# Revit family: НЕВАТОМ_Щит приточный, электрический калорифер, E, Версия 1
name_source: partatom
category: Электрооборудование
revit_build: Autodesk Revit 2017 (Build: 20170118_1100(x64)
units: mm (PartAtom-declared; Revit-internal decimal feet)

## family parameters
Всегда вертикально = Да
Заголовок OmniClass = Distribution Boards and Control Panels
Конфигурация панели = Два столбца, слева направо
На основе рабочей плоскости = Да
Номер OmniClass = 23.80.30.11.17
Общий = Нет
При загрузке вырезать с полостями = Нет
Размер круглого соединителя = Использовать диаметр
Тип детали = Щит
Точка расчета площади = Нет

## types (81) — shared parameters
ADSK_Единица измерения = шт.
ADSK_Завод-изготовитель = НЕВАТОМ
ADSK_Количество = 1
ADSK_Количество фаз = 3
ADSK_Материал = <По категории>
ф1 = 65 мм
ф2 = 144 мм
ф3 = 220 мм

## per-type parameters (varying)
| type | ADSK_Марка | ADSK_Наименование | ADSK_Напряжение | ADSK_Размер_Высота | ADSK_Размер_Длина | ADSK_Размер_Ширина | Количество ступеней нагревателя | Макс. допустимая мощность нагревателя, кВт | НЕВАТОМ_Номинальный ток двигателя | НЕВАТОМ_Ориентировочная мощность двигателя | НЕВАТОМ_Преобразователь частоты Danfoss, кВт | Отметка по умолчанию | видимость 1 | видимость 2 калорифер | видимость 3 ( 6 лампочек) | видимость 4 (4  лампочки) | видимость 5 ( 3 лампочки) | видимость 6 (5 лампочек) | кнопка |
| ABUm–Е–1–ZM-0,35-4,5/1 | ABUm–Е–1–ZM-0,35-4,5/1 | ABUm–Е–1–ZM-0,35-4,5/1 | 0 В | 650 мм | 400 мм | 200 мм | 1 мм | 4.5 | 0 А | 0 кВт |  | 1219 мм | Нет | Да | Нет | Нет | Нет | Нет | 10 мм |
| ABUm–Е–1–ZM-0,75-4,5/1 | ABUm–Е–1–ZM-0,75-4,5/1 | ABUm–Е–1–ZM-0,75-4,5/1 | 380 В | 650 мм | 400 мм | 200 мм | 1 мм | 4.5 | 0 А | 0 кВт |  | 1219 мм | Нет | Да | Нет | Нет | Нет | Нет | 10 мм |
| ABUm–E–1–ZM–0,35–6/1 | ABUm–E–1–ZM–0,35–6/1 | ABUm–E–1–ZM–0,35–6/1 | 380 В | 650 мм | 400 мм | 200 мм | 1 мм | 6 | 2 А | 0 кВт | ND–051 0,37 кВт для 3 фазы | 1219 мм | Нет | Да | Нет | Нет | Да | Нет | 10 мм |
| ABUm–E–1–ZM–0,75–6/1 | ABUm–E–1–ZM–0,75–6/1 | ABUm–E–1–ZM–0,75–6/1 | 380 В | 650 мм | 400 мм | 200 мм | 1 мм | 6 | 3 А | 0 кВт | ND–051 0,75 кВт для 3 фазы | 0 мм | Нет | Да | Нет | Нет | Да | Нет | 10 мм |
| ABUm–E–1–ZM–0,35–7,5/1 | ABUm–E–1–ZM–0,35–7,5/1 | ABUm–E–1–ZM–0,35–7,5/1 | 380 В | 650 мм | 400 мм | 300 мм | 1 мм | 7.5 | 2 А | 0 кВт | ND–051 0,37 кВт для 3 фазы | 1219 мм | Нет | Да | Нет | Нет | Да | Нет | 10 мм |
| ABUm–E–1–ZM–0,75–7,5/1 | ABUm–E–1–ZM–0,75–7,5/1 | ABUm–E–1–ZM–0,75–7,5/1 | 380 В | 650 мм | 400 мм | 200 мм | 1 мм | 7.5 | 0 А | 0 кВт |  | 1219 мм | Нет | Да | Нет | Нет | Да | Нет | 10 мм |
| ABUm–E–1–ZM–0,35–12/2 | ABUm–E–1–ZM–0,35–12/2 | ABUm–E–1–ZM–0,35–12/2 | 380 В | 650 мм | 400 мм | 200 мм | 2 мм | 12 | 2 А | 0 кВт | ND–051 0,37 кВт для 3 фазы | 1219 мм | Нет | Да | Нет | Нет | Нет | Да | 10 мм |
| ABUm–E–1–ZM–0,75–12/2 | ABUm–E–1–ZM–0,75–12/2 | ABUm–E–1–ZM–0,75–12/2 | 380 В | 650 мм | 400 мм | 200 мм | 2 мм | 12 | 3 А | 0 кВт | ND–051 0,75 кВт для 3 фазы | 1219 мм | Нет | Да | Нет | Нет | Нет | Да | 10 мм |
| ABUm–E–1–ZM–0,35–15/2 | ABUm–E–1–ZM–0,35–15/2 | ABUm–E–1–ZM–0,35–15/2 | 380 В | 650 мм | 400 мм | 200 мм | 2 мм | 15 | 2 А | 0 кВт | ND–051 0,37 кВт для 3 фазы | 1219 мм | Нет | Да | Нет | Нет | Нет | Да | 10 мм |
| ABUm–E–1–ZM–0,75–15/2 | ABUm–E–1–ZM–0,75–15/2 | ABUm–E–1–ZM–0,75–15/2 | 380 В | 650 мм | 400 мм | 200 мм | 2 мм | 15 | 3 А | 0 кВт | ND–051 0,75 кВт для 3 фазы | 1219 мм | Нет | Да | Нет | Нет | Нет | Да | 10 мм |
| ABUm–E–1–ZM–0,75–22,5/2 | ABUm–E–1–ZM–0,75–22,5/2 | ABUm–E–1–ZM–0,75–22,5/2 | 380 В | 650 мм | 400 мм | 200 мм | 2 мм | 22.5 | 3 А | 0 кВт | ND–051 0,75 кВт для 3 фазы | 1219 мм | Нет | Да | Нет | Нет | Нет | Да | 10 мм |
| ABUm–E–1–ZM–1,5–22,5/2 | ABUm–E–1–ZM–0,75–22,5/2 | ABUm–E–1–ZM–0,75–22,5/2 | 380 В | 650 мм | 400 мм | 200 мм | 2 мм | 22.5 | 4 А | 0 кВт | ND–051 1.5 кВт для 3 фазы | 1219 мм | Нет | Да | Нет | Нет | Нет | Да | 60 мм |
| ABUm–E–1–ZM–1,5–30/2 | ABUm–E–1–ZM–1,5–30/2 | ABUm–E–1–ZM–1,5–30/2 | 380 В | 650 мм | 400 мм | 200 мм | 2 мм | 30 | 4 А | 0 кВт | ND–051 1.5 кВт для 3 фазы | 1219 мм | Нет | Да | Нет | Нет | Нет | Да | 10 мм |
| ABUm–E–1–ZM–2–30/2 | ABUm–E–1–ZM–2–30/2 | ABUm–E–1–ZM–2–30/2 | 380 В | 650 мм | 400 мм | 200 мм | 2 мм | 30 | 6 А | 0 кВт | ND–051 1.5 кВт для 3 фазы | 1219 мм | Нет | Да | Нет | Нет | Нет | Да | 10 мм |
| ABUm–E–1–ZM–1,5–37,5/3 | ABUm–E–1–ZM–1,5–37,5/3 | ABUm–E–1–ZM–1,5–37,5/3 | 380 В | 800 мм | 680 мм | 200 мм | 3 мм | 37.5 | 4 А | 0 кВт | ND–051 1.5 кВт для 3 фазы | 1219 мм | Нет | Да | Нет | Да | Нет | Нет | 10 мм |
| ABUm–E–1–ZM–2–37,5/3 | ABUm–E–1–ZM–2–37,5/3 | ABUm–E–1–ZM–2–37,5/3 | 380 В | 800 мм | 680 мм | 200 мм | 3 мм | 37.5 | 6 А | 0 кВт | ND–051 2.2 кВт для 3 фазы | 1219 мм | Нет | Да | Нет | Да | Нет | Нет | 10 мм |
| ABUm–E–1–ZM–2–45/3 | ABUm–E–1–ZM–2–45/3 | ABUm–E–1–ZM–2–45/3 | 380 В | 800 мм | 680 мм | 200 мм | 3 мм | 45 | 6 А | 0 кВт | ND–051 2.2 кВт для 3 фазы | 1219 мм | Нет | Да | Нет | Нет | Нет | Нет | 10 мм |
| ABUm–E–1–ZM–4–45/3 | ABUm–E–1–ZM–4–45/3 | ABUm–E–1–ZM–4–45/3 | 380 В | 800 мм | 680 мм | 200 мм | 3 мм | 45 | 10 А | 0 кВт | ND–051 4.0 кВт для 3 фазы | 1219 мм | Нет | Да | Нет | Да | Нет | Нет | 10 мм |
| ABUm–E–1–ZM–4–60/4 | ABUm–E–1–ZM–4–60/4 | ABUm–E–1–ZM–4–60/4 | 380 В | 800 мм | 680 мм | 200 мм | 4 мм | 60 | 10 А | 0 кВт | ND–051 4.0 кВт для 3 фазы | 1219 мм | Нет | Да | Нет | Нет | Нет | Нет | 10 мм |
| ABUm–E–1–ZM–5,5–60/4 | ND–051 5,5 кВт для 3 фазы | ND–051 5,5 кВт для 3 фазы | 380 В | 800 мм | 680 мм | 200 мм | 4 мм | 60 | 0 А | 0 кВт |  | 1219 мм | Нет | Да | Нет | Нет | Нет | Нет | 10 мм |
| ABUm–E–1–ZM–4–75/5 | ABUm–E–1–ZM–4–75/5 | ABUm–E–1–ZM–4–75/5 | 380 В | 1000 мм | 800 мм | 300 мм | 5 мм | 75 | 10 А | 0 кВт | ND–051 4.0 кВт для 3 фазы | 1219 мм | Нет | Да | Нет | Нет | Нет | Нет | 10 мм |
| ABUm–E–1–ZM–5,5–75/5 | ABUm–E–1–ZM–5,5–75/5 | ABUm–E–1–ZM–5,5–75/5 | 380 В | 1000 мм | 800 мм | 300 мм | 5 мм | 75 | 13 А | 0 кВт | ND–051 5.5кВт для 3 фазы | 1219 мм | Нет | Да | Нет | Нет | Нет | Нет | 10 мм |
| ABUm–E–1–ZM–5,5–90/5 | ABUm–E–1–ZM–5,5–90/5 | ABUm–E–1–ZM–5,5–90/5 | 380 В | 1000 мм | 800 мм | 300 мм | 5 мм | 90 | 13 А | 0 кВт | ND–051 5.5 кВт для 3 фазы | 1219 мм | Нет | Да | Нет | Да | Нет | Нет | 10 мм |
| ABUm–E–1–ZM–7,5–120/5 | ABUm–E–1–ZM–7,5–120/5 | ABUm–E–1–ZM–7,5–120/5 | 380 В | 1000 мм | 800 мм | 300 мм | 5 мм | 120 | 18 А | 0 кВт | ND–051 7.5 кВт для 3 фазы | 1219 мм | Нет | Да | Нет | Да | Нет | Нет | 10 мм |
| ABUm–E–1–ZM–15–120/5 | ABUm–E–1–ZM–15–120/5 | ABUm–E–1–ZM–15–120/5 | 380 В | 1000 мм | 800 мм | 300 мм | 5 мм | 120 | 32 А | 0 кВт | ND–051 15 кВт для 3 фазы | 1219 мм | Нет | Да | Нет | Да | Нет | Нет | 10 мм |
| ABUm–E–3–Ev–0,35e–3,0e–UVi | ABUm–E–3–Ev–0,35e–3,0e–UVi | ABUm–E–3–Ev–0,35e–3,0e–UVi | 220 В | 500 мм | 450 мм | 200 мм | 0 мм | 3 | 2 А | 0 кВт | ND–051 0.75 кВт для 3 фазы | 1219 мм | Да | Да | Нет | Нет | Нет | Нет | 10 мм |
| ABUm–E–3–Ev–0,35e–4,5–UVi | ABUm–E–3–Ev–0,35e–4,5–UVi | ABUm–E–3–Ev–0,35e–4,5–UVi | 220 В | 500 мм | 450 мм | 200 мм | 0 мм | 4.5 | 2 А | 0 кВт |  | 1219 мм | Да | Да | Нет | Нет | Нет | Нет | 10 мм |
| ABUm–E–3–Ev–0,35e–6–UVi | ABUm–E–3–Ev–0,35e–6–UVi | ABUm–E–3–Ev–0,35e–6–UVi | 220 В | 500 мм | 450 мм | 200 мм | 2 мм | 6 | 2 А | 0 кВт |  | 1219 мм | Да | Да | Нет | Нет | Нет | Нет | 10 мм |
| ABUm–E–3–Ev–0,35e–7,5–UVi | ABUm–E–3–Ev–0,35e–7,5–UVi | ABUm–E–3–Ev–0,35e–7,5–UVi | 220 В | 500 мм | 450 мм | 200 мм | 0 мм | 7.5 | 2 А | 0 кВт |  | 1219 мм | Да | Да | Нет | Нет | Нет | Нет | 10 мм |
| ABUm–E–3–Ev–0,35e–12–UVi | ABUm–E–3–Ev–0,35e–12–UVi | ABUm–E–3–Ev–0,35e–12–UVi | 220 В | 500 мм | 450 мм | 200 мм | 0 мм | 12 | 2 А | 0 кВт |  | 1219 мм | Да | Да | Нет | Нет | Нет | Нет | 10 мм |
| ABUm–E–3–Ev–0,35e–15–UVi | ABUm–E–3–Ev–0,35e–15–UVi | ABUm–E–3–Ev–0,35e–15–UVi | 220 В | 500 мм | 450 мм | 200 мм | 0 мм | 15 | 2 А | 0 кВт |  | 1219 мм | Да | Да | Нет | Нет | Нет | Нет | 10 мм |
| ABUm–E–3–Ev–0,35e–18–UVi | ABUm–E–3–Ev–0,35e–18–UVi | ABUm–E–3–Ev–0,35e–18–UVi | 220 В | 500 мм | 450 мм | 200 мм | 0 мм | 18 | 2 А | 0 кВт |  | 1219 мм | Да | Да | Нет | Нет | Нет | Нет | 10 мм |
| ABUm–E–3–Ev–0,75–7,5 | ABUm–E–3–Ev–0,75–7,5 | ABUm–E–3–Ev–0,75–7,5 | 220 В | 500 мм | 450 мм | 200 мм | 0 мм | 12 | 2 А | 1 кВт | ND–051 0.75 кВт для 3 фазы | 1219 мм | Да | Да | Нет | Нет | Нет | Нет | 10 мм |
| ABUm–E–3–Ev–0,35–12 | ABUm–E–3–Ev–0,35–12 | ABUm–E–3–Ev–0,35–12 | 220 В | 500 мм | 450 мм | 200 мм | 0 мм | 12 | 1 А | 0 кВт | ND–051 0.75 кВт для 3 фазы | 1219 мм | Да | Да | Нет | Нет | Нет | Нет | 10 мм |
| ABUm–E–3–Ev–0,35–3,0e | ABUm–E–3–Ev–0,35–3,0e | ABUm–E–3–Ev–0,35–3,0e | 380 В | 500 мм | 450 мм | 200 мм | 0 мм | 3 | 1 А | 0 кВт | ND–051 0.75 кВт для 3 фазы | 1219 мм | Да | Да | Нет | Нет | Нет | Нет | 10 мм |
| ABUm–E–3–Ev–0,35–4,5 | ABUm–E–3–Ev–0,35–4,5 | ABUm–E–3–Ev–0,35–4,5 | 380 В | 500 мм | 450 мм | 200 мм | 0 мм | 4.5 | 1 А | 0 кВт | ND–051 0.75 кВт для 3 фазы | 1219 мм | Да | Да | Нет | Нет | Нет | Нет | 10 мм |
| ABUm–E–3–Ev–0,75–4,5 | ABUm–E–3–Ev–0,75–4,5 | ABUm–E–3–Ev–0,75–4,5 | 380 В | 500 мм | 450 мм | 200 мм | 0 мм | 4.5 | 0 А | 0 кВт | ND–051 0.75 кВт для 3 фазы | 1219 мм | Да | Да | Нет | Нет | Нет | Нет | 10 мм |
| ABUm–E–3–Ev–0,35–6 | ABUm–E–3–Ev–0,35–6 | ABUm–E–3–Ev–0,35–6 | 380 В | 500 мм | 450 мм | 200 мм | 0 мм | 6 | 1 А | 0 кВт | ND–051 0.75 кВт для 3 фазы | 1219 мм | Да | Да | Нет | Нет | Нет | Нет | 10 мм |
| ABUm–E–3–Ev–0,75–6 | ABUm–E–3–Ev–0,75–6 | ABUm–E–3–Ev–0,75–6 | 380 В | 500 мм | 450 мм | 200 мм | 0 мм | 6 | 0 А | 0 кВт |  | 1219 мм | Да | Да | Нет | Нет | Нет | Нет | 10 мм |
| ABUm–E–3–Ev–0,35–7,5 | ABUm–E–3–Ev–0,35–7,5 | ABUm–E–3–Ev–0,35–7,5 | 380 В | 500 мм | 450 мм | 200 мм | 0 мм | 7.5 | 2 А | 0 кВт | ND–051 0.75 кВт для 3 фазы | 1219 мм | Да | Да | Нет | Нет | Нет | Нет | 10 мм |
| ABUm–E–3–Ev–0,35–15 | ABUm–E–3–Ev–0,35–15 | ABUm–E–3–Ev–0,35–15 | 380 В | 500 мм | 450 мм | 200 мм | 1 мм | 15 | 0 А | 0 кВт | ND–051 0.75 кВт для 3 фазы | 1219 мм | Да | Да | Нет | Нет | Нет | Нет | 10 мм |
| ABUm–E–3–Ev–0,75–15 | ABUm–E–3–Ev–0,75–15 | ABUm–E–3–Ev–0,75–15 | 380 В | 500 мм | 450 мм | 200 мм | 0 мм | 15 | 2 А | 1 кВт | ND–051 0.75 кВт для 3 фазы | 1219 мм | Да | Да | Нет | Нет | Нет | Нет | 10 мм |
| ABUm–E–3–Ev–0,75–22,5 | ABUm–E–3–Ev–0,75–22,5 | ABUm–E–3–Ev–0,75–22,5 | 380 В | 500 мм | 450 мм | 200 мм | 0 мм | 22.5 | 2 А | 2 кВт | ND–051 1.5 кВт для 3 фазы | 1219 мм | Да | Да | Нет | Нет | Нет | Нет | 10 мм |
| ABUm–E–3–Ev–1,5–22,5 | ABUm–E–3–Ev–1,5–22,5 | ABUm–E–3–Ev–1,5–22,5 | 380 В | 500 мм | 450 мм | 200 мм | 0 мм | 22.5 | 4 А | 2 кВт | ND–051 1.5 кВт для 3 фазы | 1219 мм | Да | Да | Нет | Нет | Нет | Нет | 10 мм |
| ABUm–E–3–Ev–1,5–30 | ABUm–E–3–Ev–1,5–30 | ABUm–E–3–Ev–1,5–30 | 380 В | 500 мм | 450 мм | 200 мм | 0 мм | 30 | 4 А | 2 кВт | ND–051 1.5 кВт для 3 фазы | 1219 мм | Да | Да | Нет | Нет | Нет | Нет | 10 мм |
| ABUm–E–3–EV–2,2–30 | ABUm–E–3–Ev–1,5–30 | ABUm–E–3–Ev–1,5–30 | 380 В | 500 мм | 450 мм | 200 мм | 0 мм | 30 | 5 А | 2 кВт | ND–051 2.2 кВт для 3 фазы | 1219 мм | Да | Да | Нет | Нет | Нет | Нет | 10 мм |
| ABUm–E–4–0,35–4,5/1 | ABUm–E–4–0,35–4,5/1 | ABUm–E–4–0,35–4,5/1 | 380 В | 500 мм | 450 мм | 200 мм | 0 мм | 4.5 | 1 А | 0 кВт | ND–051 0.75 кВт для 3 фазы | 1219 мм | Нет | Нет | Да | Нет | Нет | Нет | 10 мм |
| ABUm–E–4–0,75–4,5/1 | ABUm–E–4–0,35–4,5/1 | ABUm–E–4–0,35–4,5/1 | 380 В | 500 мм | 450 мм | 200 мм | 0 мм | 4.5 | 2 А | 1 кВт | ND–051 0.75 кВт для 3 фазы | 1219 мм | Нет | Нет | Да | Нет | Нет | Нет | 10 мм |
| ABUm–E–4–0,35–6/1 | ABUm–E–4–0,35–6/1 | ABUm–E–4–0,35–6/1 | 380 В | 500 мм | 450 мм | 200 мм | 0 мм | 6 | 1 А | 0 кВт | ND–051 0.75 кВт для 3 фазы | 1219 мм | Нет | Нет | Да | Нет | Нет | Нет | 10 мм |
| ABUm–E–4–0,75–6/1 | ABUm–E–4–0,75–6/1 | ABUm–E–4–0,75–6/1 | 380 В | 500 мм | 450 мм | 200 мм | 0 мм | 6 | 2 А | 1 кВт | ND–051 0.75 кВт для 3 фазы | 1219 мм | Нет | Нет | Да | Нет | Нет | Нет | 10 мм |
| ABUm–E–4–0,35–7,5/1 | ABUm–E–4–0,35–7,5/1 | ABUm–E–4–0,35–7,5/1 | 380 В | 500 мм | 450 мм | 200 мм | 0 мм | 7.5 | 0 А | 0 кВт | ND–051 0.75 кВт для 3 фазы | 1219 мм | Нет | Нет | Да | Нет | Нет | Нет | 10 мм |
| ABUm–E–4–0,75–7,5/1 | ABUm–E–4–0,35–7,5/1 | ABUm–E–4–0,35–7,5/1 | 380 В | 500 мм | 450 мм | 200 мм | 0 мм | 7.5 | 1 А | 1 кВт | ND–051 0.75 кВт для 3 фазы | 1219 мм | Нет | Нет | Да | Нет | Нет | Нет | 10 мм |
| ABUm–E–4–0,35–12/2 | ABUm–E–4–0,35–12/2 | ABUm–E–4–0,35–12/2 | 380 В | 500 мм | 450 мм | 200 мм | 0 мм | 12 | 1 А | 0 кВт | ND–051 0.75 кВт для 3 фазы | 1219 мм | Нет | Нет | Да | Нет | Нет | Нет | 10 мм |
| ABUm–E–4–0,35–15/2 | ABUm–E–4–0,35–15/2 | ABUm–E–4–0,35–15/2 | 380 В | 500 мм | 450 мм | 200 мм | 0 мм | 15 | 1 А | 0 кВт | ND–051 0.75 кВт для 3 фазы | 1219 мм | Нет | Нет | Да | Нет | Нет | Нет | 10 мм |
| ABUm–E–4–0,75–15/2 | ABUm–E–4–0,75–15/2 | ABUm–E–4–0,75–15/2 | 380 В | 500 мм | 450 мм | 200 мм | 0 мм | 15 | 2 А | 1 кВт | ND–051 0.75 кВт для 3 фазы | 1219 мм | Нет | Нет | Да | Нет | Нет | Нет | 10 мм |
| ABUm–E–4–0,75–22,5/2 | ABUm–E–4–0,75–22,5/2 | ABUm–E–4–0,75–22,5/2 | 380 В | 500 мм | 450 мм | 200 мм | 0 мм | 22.5 | 1 А | 1 кВт | ND–051 0.75 кВт для 3 фазы | 1219 мм | Нет | Нет | Да | Нет | Нет | Нет | 10 мм |
| ABUm–E–4–1,5–22,5/2 | ABUm–E–4–1,5–22,5/2 | ABUm–E–4–1,5–22,5/2 | 380 В | 500 мм | 450 мм | 200 мм | 0 мм | 22.5 | 4 А | 2 кВт | ND–051 1.5 кВт для 3 фазы | 1219 мм | Нет | Нет | Да | Нет | Нет | Нет | 10 мм |
| ABUm–E–4–1,5–30/2 | ABUm–E–4–1,5–30/2 | ABUm–E–4–1,5–30/2 | 380 В | 500 мм | 450 мм | 200 мм | 0 мм | 30 | 4 А | 2 кВт | ND–051 1.5 кВт для 3 фазы | 1219 мм | Нет | Нет | Да | Нет | Нет | Нет | 10 мм |
| ABUm–E–4–2,2–30/2 | ABUm–E–4–2,2–30/2 | ABUm–E–4–2,2–30/2 | 380 В | 500 мм | 450 мм | 200 мм | 0 мм | 30 | 5 А | 2 кВт | ND–051 2.2 кВт для 3 фазы | 1219 мм | Нет | Нет | Да | Нет | Нет | Нет | 10 мм |
| ABUm–E–4–1,5–37,5/3 | ABUm–E–4–1,5–37,5/3 | ABUm–E–4–1,5–37,5/3 | 380 В | 650 мм | 400 мм | 200 мм | 0 мм | 37.5 | 4 А | 2 кВт | ND–051 1.5 кВт для 3 фазы | 1219 мм | Нет | Нет | Да | Нет | Нет | Нет | 10 мм |
| ABUm–E–4–2,2–37,5/3 | ABUm–E–4–2,2–37,5/3 | ABUm–E–4–2,2–37,5/3 | 380 В | 650 мм | 400 мм | 200 мм | 0 мм | 37.5 | 5 А | 2 кВт | ND–051 2.2 кВт для 3 фазы | 1219 мм | Нет | Нет | Да | Нет | Нет | Нет | 10 мм |
| ABUm–E–4–2,2–45/3 | ABUm–E–4–2,2–45/3 | ABUm–E–4–2,2–45/3 | 380 В | 650 мм | 400 мм | 200 мм | 0 мм | 45 | 9 А | 4 кВт | ND–051 2.2 кВт для 3 фазы | 1219 мм | Нет | Нет | Да | Нет | Нет | Нет | 10 мм |
| ABUm–E–4–4–45/3 | ABUm–E–4–4–45/3 | ABUm–E–4–4–45/3 | 380 В | 650 мм | 400 мм | 200 мм | 0 мм | 45 | 9 А | 4 кВт | ND–051 4.0 кВт для 3 фазы | 1219 мм | Нет | Нет | Да | Нет | Нет | Нет | 10 мм |
| ABUm–E–4–4–60/4 | ABUm–E–4–4–60/4 | ABUm–E–4–4–60/4 | 380 В | 800 мм | 600 мм | 200 мм | 0 мм | 60 | 9 А | 4 кВт | ND–051 4.0 кВт для 3 фазы | 1219 мм | Нет | Нет | Да | Нет | Нет | Нет | 10 мм |
| ABUm–E–4–5,5–60/4 | ABUm–E–4–5,5–60/4 | ABUm–E–4–5,5–60/4 | 380 В | 800 мм | 600 мм | 200 мм | 0 мм | 60 | 11 А | 0 кВт | ND–051 5.5 кВт для 3 фазы | 1219 мм | Нет | Нет | Да | Нет | Нет | Нет | 10 мм |
| ABUm–E–4–4–75/5 | ABUm–E–4–4–75/5 | ABUm–E–4–4–75/5 | 380 В | 800 мм | 600 мм | 200 мм | 0 мм | 75 | 9 А | 4 кВт | ND–051 4.0 кВт для 3 фазы | 1219 мм | Нет | Нет | Да | Нет | Нет | Нет | 10 мм |
| ABUm–E–4–5,5–75/5 | ABUm–E–4–5,5–75/5 | ABUm–E–4–5,5–75/5 | 380 В | 800 мм | 600 мм | 200 мм | 0 мм | 75 | 11 А | 6 кВт | ND–051 5.5 кВт для 3 фазы | 1219 мм | Нет | Нет | Да | Нет | Нет | Нет | 10 мм |
| ABUm–E–4–5,5–90/5 | ABUm–E–4–5,5–90/5 | ABUm–E–4–5,5–90/5 | 380 В | 800 мм | 600 мм | 200 мм | 0 мм | 90 | 11 А | 6 кВт | ND–051 5.5 кВт для 3 фазы | 1219 мм | Нет | Нет | Да | Нет | Нет | Нет | 10 мм |
| ABUm–E–4–7,5–120/5 | ABUm–E–4–7,5–120/5 | ABUm–E–4–7,5–120/5 | 380 В | 800 мм | 600 мм | 200 мм | 0 мм | 120 | 16 А | 8 кВт | ND–051 7.5 кВт для 3 фазы | 1219 мм | Нет | Нет | Да | Нет | Нет | Нет | 10 мм |
| ABUm–E–1–Z–0,8e–4,5–PZ/UVi | ABUm–E–1–Z–0,8e–4,5–PZ/UVi | ABUm–E–1–Z–0,8e–4,5–PZ/UVi | 220 В | 500 мм | 450 мм | 200 мм | 0 мм | 4.5 | 2 А | 1 кВт |  | 1219 мм | Нет | Да | Нет | Нет | Нет | Нет | 10 мм |
| ABUm–E–1–Z–0,35e–6–PZ/UVi | ABUm–E–1–Z–0,35e–6–PZ/UVi | ABUm–E–1–Z–0,35e–6–PZ/UVi | 220 В | 500 мм | 450 мм | 200 мм | 0 мм | 6 | 2 А | 0 кВт |  | 1219 мм | Нет | Да | Нет | Да | Нет | Нет | 10 мм |
| ABUm–E–1–Z–0,8e–6–PZ/UVi | ABUm–E–1–Z–0,8e–6–PZ/UVi | ABUm–E–1–Z–0,8e–6–PZ/UVi | 220 В | 500 мм | 450 мм | 200 мм | 0 мм | 6 | 4 А | 0 кВт |  | 1219 мм | Нет | Да | Нет | Нет | Нет | Нет | 10 мм |
| ABUm–E–1–Z–0,8e–7,5–PZ/UVi | ABUm–E–1–Z–0,8e–7,5–PZ/UVi | ABUm–E–1–Z–0,8e–7,5–PZ/UVi | 220 В | 500 мм | 450 мм | 200 мм | 0 мм | 7.5 | 4 А | 0 кВт |  | 1219 мм | Нет | Да | Нет | Нет | Нет | Нет | 10 мм |
| ABUm–E–1–Z–0,35e–12–PZ/UVi | ABUm–E–1–Z–0,35e–12–PZ/UVi | ABUm–E–1–Z–0,35e–12–PZ/UVi | 220 В | 500 мм | 450 мм | 200 мм | 0 мм | 12 | 2 А | 0 кВт |  | 1219 мм | Нет | Да | Нет | Нет | Нет | Нет | 10 мм |
| ABUm–E–1–Z–0,8e–12–PZ/UVi | ABUm–E–1–Z–0,8e–12–PZ/UVi | ABUm–E–1–Z–0,8e–12–PZ/UVi | 220 В | 500 мм | 450 мм | 200 мм | 0 мм | 12 | 0 А | 1 кВт |  | 1219 мм | Нет | Да | Нет | Да | Нет | Нет | 10 мм |
| ABUm–E–1–Z–0,35e–15–PZ/UVi | ABUm–E–1–Z–0,8e–22,5–PZ/UVi | ABUm–E–1–Z–0,8e–22,5–PZ/UVi | 220 В | 500 мм | 450 мм | 200 мм | 0 мм | 15 | 4 А | 1 кВт |  | 1219 мм | Нет | Да | Нет | Нет | Нет | Нет | 10 мм |
| ABUm–E–1–ZM–0,35–4,5/1 | ABUm–E–1–ZM–0,35–4,5/1 | ABUm–E–1–ZM–0,35–4,5/1 | 380 В | 650 мм | 400 мм | 200 мм | 1 мм | 4.5 | 2 А | 0 кВт | ND–051 0,37 кВт для 3 фазы | 0 мм | Нет | Да | Нет | Нет | Да | Нет | 10 мм |
| ABUm–E–1–ZM–0,75–4,5/1 | ABUm–E–1–ZM–0,75–4,5/1 | ABUm–E–1–ZM–0,75–4,5/1 | 380 В | 650 мм | 400 мм | 200 мм | 1 мм | 4.5 | 3 А | 1 кВт | ND–051 0,75 кВт для 3 фазы | 1219 мм | Нет | Да | Нет | Нет | Да | Нет | 10 мм |
| ABUm–E–1–ZM–7,5–90/5 | ABUm–E–1–ZM–7,5–90/5 | ABUm–E–1–ZM–7,5–90/5 | 380 В | 1000 мм | 800 мм | 300 мм | 5 мм | 90 | 0 А | 0 кВт |  | 1219 мм | Нет | Да | Нет | Да | Нет | Нет | 10 мм |
| ABUm–E–1–Z–0,8e–15–PZ/UVi | ABUm–E–1–Z–0,8e–15–PZ/UVi | ABUm–E–1–Z–0,8e–15–PZ/UVi | 220 В | 500 мм | 450 мм | 200 мм | 0 мм | 15 | 4 А | 1 кВт |  | 1219 мм | Нет | Да | Нет | Нет | Нет | Нет | 10 мм |
| ABUm–E–1–Z–0,8e–22,5–PZ/UVi | ABUm–E–1–Z–0,8e–22,5–PZ/UVi | ABUm–E–1–Z–0,8e–22,5–PZ/UVi | 220 В | 500 мм | 450 мм | 200 мм | 0 мм | 22.5 | 0 А | 0 кВт |  | 1219 мм | Нет | Да | Нет | Нет | Нет | Нет | 10 мм |
